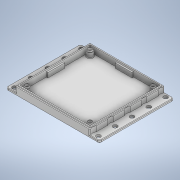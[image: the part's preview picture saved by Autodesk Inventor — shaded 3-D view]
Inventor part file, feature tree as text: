
AUTODESK INVENTOR PART (.ipt)
format: ipt  version: 2020 (Build 240168000, 168)  size: 241,152 bytes
history: native  units: mm
features: other x1, chamfer x1
ambient origin geometry x8: Origin, YZ Plane, XZ Plane, XY Plane, X Axis, Y Axis, Z Axis, Center Point
bodies: Body1 (feature_tree)
feature tree (2):
  other  "Твердое тело1"
  chamfer  "Chamfer1"  [1 undecoded]
note: 1 required parameter value undecoded (feature->parameter linkage not recoverable at this tier; creation-order binding heuristic only, values carry confidence <= 0.55)
